annotation { "Feature Type Name" : "Feature", "Feature Type Description" : "" }
export const myFeature = defineFeature(function(context is Context, id is Id, definition is map)
    precondition{}
    {
        {
            var Q0;
            Q0=qCreatedBy(makeId("Top.planeOp"),FACE);
            var sketch = newSketch(context, id + "F0", { "sketchPlane" : qUnion([Q0])});
            skLineSegment(sketch, "E0.top", {"start": v(38, 27) * mm, "end": v(0, 27) * mm});
            skLineSegment(sketch, "E0.left", {"start": v(42, 0) * mm, "end": v(42, 23) * mm});
            skPoint(sketch, "E0.middle", {"position": v(0, 0) * mm});
            skArc(sketch, "E1", {"start": v(42, 23) * mm, "mid": v(40.83, 25.83) * mm, "end": v(38, 27) * mm});
            skLineSegment(sketch, "E2", {"start": v(0, 0) * mm, "end": v(0, 27) * mm});
            skLineSegment(sketch, "E3", {"start": v(0, 0) * mm, "end": v(42, 0) * mm});
            skPoint(sketch, "E0.right.end.orphan", {"position": v(-42, 27) * mm});
            skPoint(sketch, "E0.bottom.end.orphan", {"position": v(-42, -27) * mm});
            skPoint(sketch, "E4.orphan", {"position": v(42, -27) * mm});
            skPoint(sketch, "E5.orphan", {"position": v(42, 27) * mm});
            skArc(sketch, "E6.MirrorCS", {"start": v(-42, 23) * mm, "mid": v(-40.83, 25.83) * mm, "end": v(-38, 27) * mm});
            skLineSegment(sketch, "E7.MirrorCS", {"start": v(-38, 27) * mm, "end": v(0, 27) * mm});
            skLineSegment(sketch, "E8.MirrorCS", {"start": v(-42, 0) * mm, "end": v(-42, 23) * mm});
            skLineSegment(sketch, "E9.MirrorCS", {"start": v(0, 0) * mm, "end": v(-42, 0) * mm});
            skArc(sketch, "E10.MirrorCS", {"start": v(-42, -23) * mm, "mid": v(-40.83, -25.83) * mm, "end": v(-38, -27) * mm});
            skArc(sketch, "E11.MirrorCS", {"start": v(42, -23) * mm, "mid": v(40.83, -25.83) * mm, "end": v(38, -27) * mm});
            skLineSegment(sketch, "E12.MirrorCS", {"start": v(0, 0) * mm, "end": v(0, -27) * mm});
            skLineSegment(sketch, "E13.MirrorCS", {"start": v(42, 0) * mm, "end": v(42, -23) * mm});
            skLineSegment(sketch, "E14.MirrorCS", {"start": v(-38, -27) * mm, "end": v(0, -27) * mm});
            skLineSegment(sketch, "E15.MirrorCS", {"start": v(-42, 0) * mm, "end": v(-42, -23) * mm});
            skLineSegment(sketch, "E16.MirrorCS", {"start": v(38, -27) * mm, "end": v(0, -27) * mm});
            skSolve(sketch);
        }
        {
            var Q0;
            Q0 = qSketchRegion(id + "F0", true);
            extrude(context, id + "F1", {"entities" : qUnion([Q0]), "depth" : .75 * mm});
        }
        {
            var Q0;
            Q0=qCreatedBy(makeId("Top.planeOp"),FACE);
            var sketch = newSketch(context, id + "F2", { "sketchPlane" : qUnion([Q0])});
            skText(sketch, "E17", { "text": "Henry Terefenko", "fontName": "OpenSans-Bold.ttf"});
            skText(sketch, "E18", { "text": "Engineer/Maker", "fontName": "OpenSans-Bold.ttf"});
            skText(sketch, "E19", { "text": "<email>", "fontName": "OpenSans-Bold.ttf"});
            const initialGuessF2  = {"E17": [-0.03791, 0.00886, 1, 0, 0.0065], "E18": [-0.0306, -0.00241, 1, 0, 0.0055], "E19": [-0.03846, -0.01685, 1, 0, 0.0038]};
            skSetInitialGuess(sketch, initialGuessF2);
            skSolve(sketch);
        }
        {
            var Q0;
            Q0 = qSketchRegion(id + "F2", true);
            extrude(context, id + "F3", {"entities" : qUnion([Q0]), "operationType" : NewBodyOperationType.ADD, "depth" : 1.25 * mm});
        }
        {
            var Q0;
            Q0=qCreatedBy(makeId("Top.planeOp"),FACE);
            var sketch = newSketch(context, id + "F4", { "sketchPlane" : qUnion([Q0])});
            skLineSegment(sketch, "E20.top", {"start": v(38, 27) * mm, "end": v(0, 27) * mm});
            skLineSegment(sketch, "E20.left", {"start": v(42, 0) * mm, "end": v(42, 23) * mm});
            skPoint(sketch, "E20.middle", {"position": v(0, 0) * mm});
            skArc(sketch, "E21", {"start": v(42, 23) * mm, "mid": v(40.83, 25.83) * mm, "end": v(38, 27) * mm});
            skLineSegment(sketch, "E22", {"start": v(0, 26) * mm, "end": v(0, 27) * mm});
            skLineSegment(sketch, "E23", {"start": v(41, 0) * mm, "end": v(42, 0) * mm});
            skPoint(sketch, "E24.orphan", {"position": v(42, 27) * mm});
            skArc(sketch, "E25", {"start": v(41, 23) * mm, "mid": v(40.12, 25.12) * mm, "end": v(38, 26) * mm});
            skLineSegment(sketch, "E26", {"start": v(38, 26) * mm, "end": v(0, 26) * mm});
            skLineSegment(sketch, "E27", {"start": v(41, 23) * mm, "end": v(41, 0) * mm});
            skLineSegment(sketch, "E28.MirrorCS", {"start": v(-38, 27) * mm, "end": v(0, 27) * mm});
            skLineSegment(sketch, "E29.MirrorCS", {"start": v(-38, 26) * mm, "end": v(0, 26) * mm});
            skArc(sketch, "E30.MirrorCS", {"start": v(-41, 23) * mm, "mid": v(-40.12, 25.12) * mm, "end": v(-38, 26) * mm});
            skArc(sketch, "E31.MirrorCS", {"start": v(-42, 23) * mm, "mid": v(-40.83, 25.83) * mm, "end": v(-38, 27) * mm});
            skLineSegment(sketch, "E32.MirrorCS", {"start": v(-42, 0) * mm, "end": v(-42, 23) * mm});
            skLineSegment(sketch, "E33.MirrorCS", {"start": v(-41, 23) * mm, "end": v(-41, 0) * mm});
            skLineSegment(sketch, "E34.MirrorCS", {"start": v(41, -23) * mm, "end": v(41, 0) * mm});
            skLineSegment(sketch, "E35.MirrorCS", {"start": v(42, 0) * mm, "end": v(42, -23) * mm});
            skArc(sketch, "E36.MirrorCS", {"start": v(41, -23) * mm, "mid": v(40.12, -25.12) * mm, "end": v(38, -26) * mm});
            skArc(sketch, "E37.MirrorCS", {"start": v(42, -23) * mm, "mid": v(40.83, -25.83) * mm, "end": v(38, -27) * mm});
            skLineSegment(sketch, "E38.MirrorCS", {"start": v(38, -26) * mm, "end": v(0, -26) * mm});
            skLineSegment(sketch, "E39.MirrorCS", {"start": v(38, -27) * mm, "end": v(0, -27) * mm});
            skLineSegment(sketch, "E40.MirrorCS", {"start": v(-38, -26) * mm, "end": v(0, -26) * mm});
            skLineSegment(sketch, "E41.MirrorCS", {"start": v(-38, -27) * mm, "end": v(0, -27) * mm});
            skArc(sketch, "E42.MirrorCS", {"start": v(-42, -23) * mm, "mid": v(-40.83, -25.83) * mm, "end": v(-38, -27) * mm});
            skArc(sketch, "E43.MirrorCS", {"start": v(-41, -23) * mm, "mid": v(-40.12, -25.12) * mm, "end": v(-38, -26) * mm});
            skLineSegment(sketch, "E44.MirrorCS", {"start": v(-42, 0) * mm, "end": v(-42, -23) * mm});
            skLineSegment(sketch, "E45.MirrorCS", {"start": v(-41, -23) * mm, "end": v(-41, 0) * mm});
            skSolve(sketch);
        }
        {
            var Q0;
            Q0 = qSketchRegion(id + "F4", true);
            extrude(context, id + "F5", {"entities" : qUnion([Q0]), "operationType" : NewBodyOperationType.ADD, "depth" : 1.25 * mm});
        }
    });